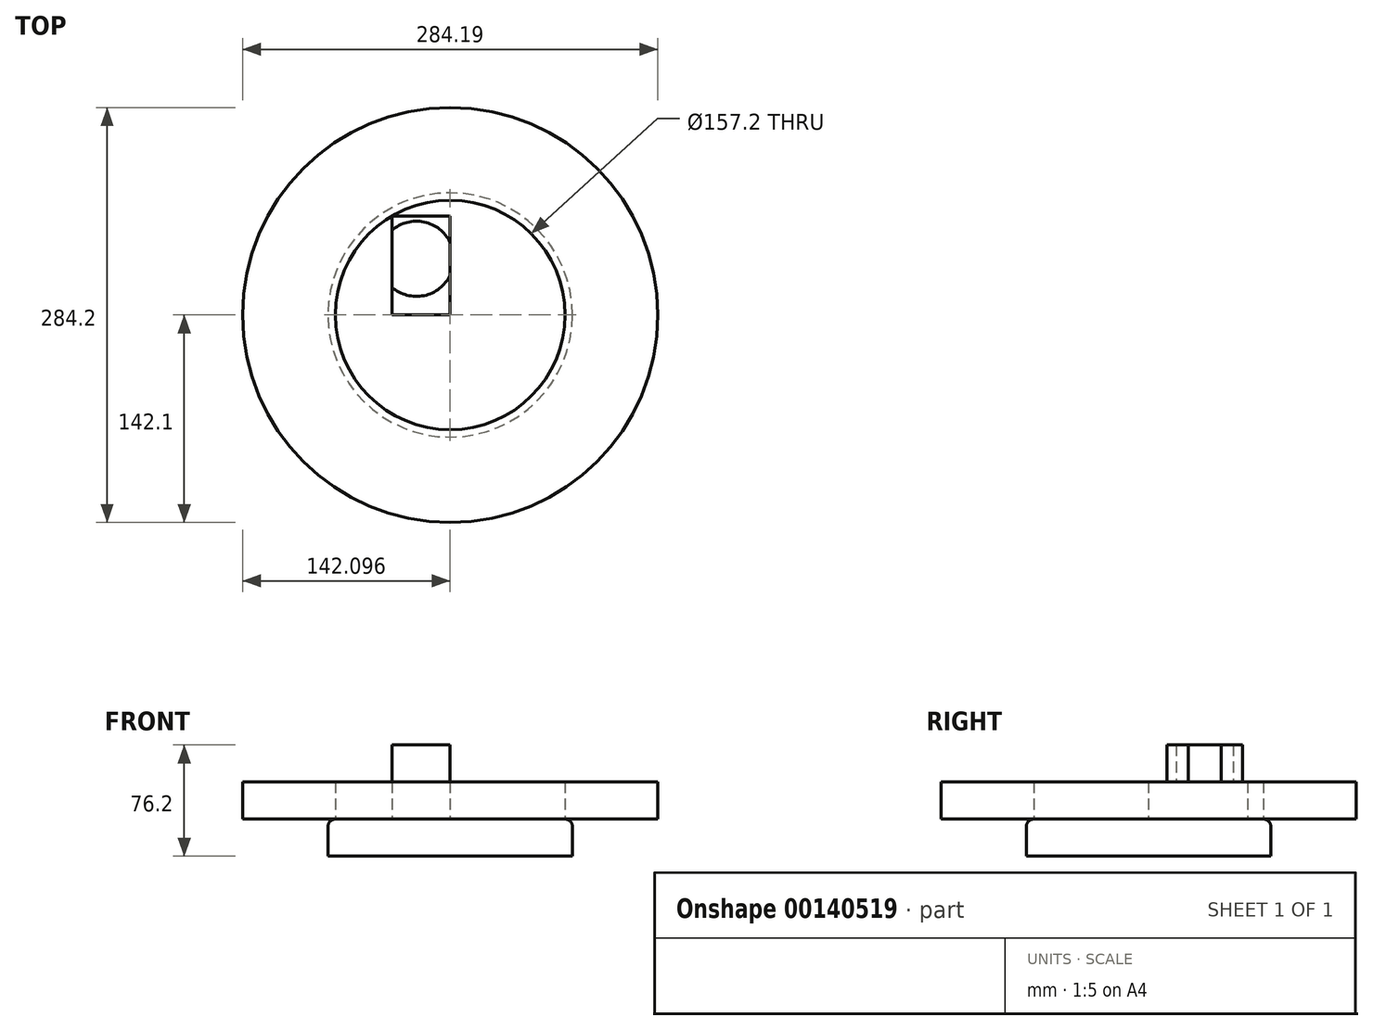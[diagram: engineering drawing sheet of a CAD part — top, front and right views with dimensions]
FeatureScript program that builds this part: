
annotation { "Feature Type Name" : "Feature", "Feature Type Description" : "" }
export const myFeature = defineFeature(function(context is Context, id is Id, definition is map)
    precondition{}
    {
        {
            var Q0;
            Q0=qCreatedBy(makeId("Top.planeOp"),FACE);
            var sketch = newSketch(context, id + "F0", { "sketchPlane" : qUnion([Q0])});
            skCircle(sketch, "E0", {"center": v(-32.24, 104.3) * mm, "radius": 83.68 * mm});
            skSolve(sketch);
        }
        {
            var Q0;
            Q0=makeQuery(id+"F0.imprint","IMPRINT",FACE,{"disambiguationData":[TD([[makeQuery(id+"F0.imprint","IMPRINT",EDGE,{"derivedFrom":sQuery(id+"F0.wireOp",EDGE,"E0")}),1.0]])]});
            extrude(context, id + "F9", {"entities" : qUnion([Q0]), "depth" : 25.4 * mm});
        }
        {
            var Q0;
            Q0=makeQuery(id+"F9.opExtrude","CAP_EDGE",EDGE,{"disambiguationData":[OSD([sQuery(id+"F0.wireOp",EDGE,"E0")])],"isStart":false});
            fillet(context, id + "F1", {"entities" : qUnion([Q0]), "radius" : 5.08 * mm, "tangentPropagation" : true, "allowEdgeOverflow" : false});
        }
        {
            var Q0;
            Q0=makeQuery(id+"F9.opExtrude","CAP_FACE",FACE,{"disambiguationData":[OSD([sQuery(id+"F0.wireOp",EDGE,"E0")])],"isStart":false});
            var sketch = newSketch(context, id + "F2", { "sketchPlane" : qUnion([Q0])});
            skCircle(sketch, "E1", {"center": v(-32.24, 104.3) * mm, "radius": 142.1 * mm});
            skSolve(sketch);
        }
        {
            var Q0;
            Q0=makeQuery(id+"F2.imprint","IMPRINT",FACE,{"disambiguationData":[TD([[makeQuery(id+"F2.imprint","IMPRINT",EDGE,{"derivedFrom":sQuery(id+"F2.wireOp",EDGE,"E1")}),1.0]])]});
            extrude(context, id + "F3", {"entities" : qUnion([Q0]), "operationType" : NewBodyOperationType.ADD, "depth" : 25.4 * mm});
        }
        {
            var Q0;
            Q0=makeQuery(id+"F9.opExtrude","CAP_FACE",FACE,{"disambiguationData":[OSD([sQuery(id+"F0.wireOp",EDGE,"E0")])],"isStart":false});
            var sketch = newSketch(context, id + "F4", { "sketchPlane" : qUnion([Q0])});
            skLineSegment(sketch, "E2.bottom", {"start": v(-32.24, 104.3) * mm, "end": v(-72.17, 104.3) * mm});
            skLineSegment(sketch, "E2.top", {"start": v(-32.24, 172.01) * mm, "end": v(-72.17, 172.01) * mm});
            skLineSegment(sketch, "E2.left", {"start": v(-32.24, 104.3) * mm, "end": v(-32.24, 172.01) * mm});
            skLineSegment(sketch, "E2.right", {"start": v(-72.17, 104.3) * mm, "end": v(-72.17, 172.01) * mm});
            skSolve(sketch);
        }
        {
            var Q0;
            Q0=makeQuery(id+"F4.imprint","IMPRINT",FACE,{"disambiguationData":[TD([[makeQuery(id+"F4.imprint","IMPRINT",EDGE,{"derivedFrom":sQuery(id+"F4.wireOp",EDGE,"E2.bottom")}),-1.0]])]});
            extrude(context, id + "F5", {"entities" : qUnion([Q0]), "operationType" : NewBodyOperationType.ADD, "depth" : 25.4 * mm});
        }
        {
            var Q0;
            Q0=makeQuery(id+"F5.opExtrude","CAP_FACE",FACE,{"disambiguationData":[OSD([sQuery(id+"F4.wireOp",EDGE,"E2.bottom"),sQuery(id+"F4.wireOp",EDGE,"E2.top"),sQuery(id+"F4.wireOp",EDGE,"E2.left"),sQuery(id+"F4.wireOp",EDGE,"E2.right")])],"isStart":false});
            var sketch = newSketch(context, id + "F6", { "sketchPlane" : qUnion([Q0])});
            skCircle(sketch, "E3", {"center": v(-55.37, 142.78) * mm, "radius": 25.74 * mm});
            skSolve(sketch);
        }
        {
            var Q0;
            {var subQ0=sQuery(id+"F6.wireOp",EDGE,"E3");var subQ1=makeQuery(id+"F5.opExtrude","CAP_EDGE",EDGE,{"disambiguationData":[OSD([sQuery(id+"F4.wireOp",EDGE,"E2.right")])],"isStart":false});var subQ2=makeQuery(id+"F6.imprint","INTERSECT",VERTEX,{"disambiguationData":[OD(0.0)],"derivedFrom":[subQ1,subQ0]});Q0=makeQuery(id+"F6.imprint","IMPRINT",FACE,{"disambiguationData":[TD([[makeQuery(id+"F6.imprint","IMPRINT",EDGE,{"disambiguationData":[TD([[subQ2,1.0]])],"derivedFrom":subQ0}),1.0]])]});}
            extrude(context, id + "F7", {"entities" : qUnion([Q0]), "operationType" : NewBodyOperationType.ADD, "depth" : 25.4 * mm});
        }
    });
